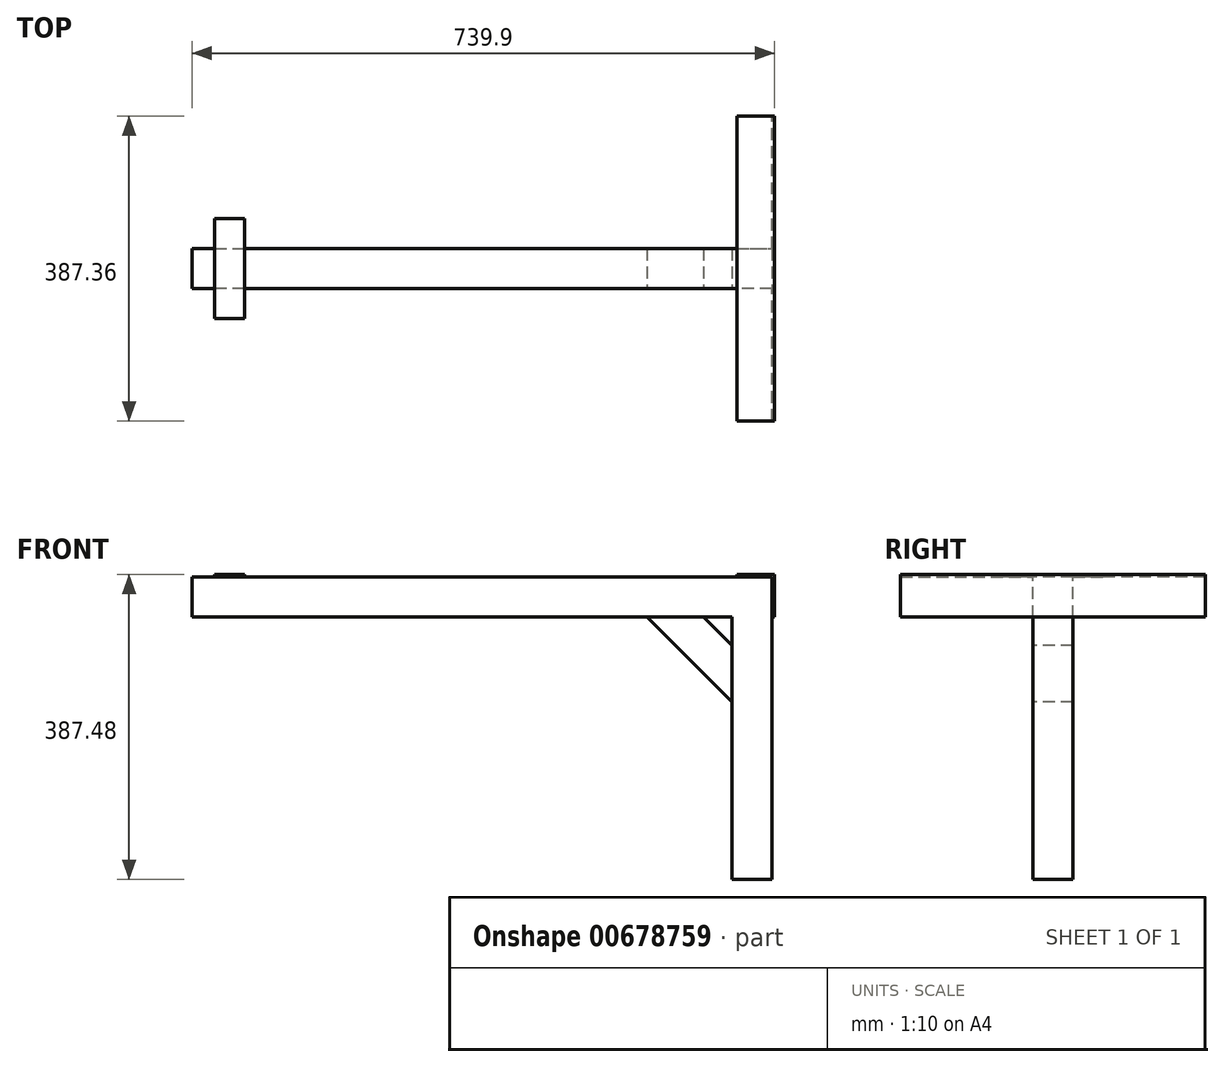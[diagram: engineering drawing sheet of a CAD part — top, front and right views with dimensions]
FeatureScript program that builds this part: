
annotation { "Feature Type Name" : "Feature", "Feature Type Description" : "" }
export const myFeature = defineFeature(function(context is Context, id is Id, definition is map)
    precondition{}
    {
        {
            var Q0;
            Q0=qCreatedBy(makeId("Top.planeOp"),FACE);
            var sketch = newSketch(context, id + "F0", { "sketchPlane" : qUnion([Q0])});
            skLineSegment(sketch, "E0.bottom", {"start": v(25.4, 193.68) * mm, "end": v(-25.4, 193.68) * mm});
            skLineSegment(sketch, "E0.top", {"start": v(25.4, -193.68) * mm, "end": v(-25.4, -193.68) * mm});
            skLineSegment(sketch, "E0.left", {"start": v(25.4, 193.68) * mm, "end": v(25.4, -193.68) * mm});
            skLineSegment(sketch, "E0.right", {"start": v(-25.4, 193.68) * mm, "end": v(-25.4, -193.68) * mm});
            skPoint(sketch, "E0.middle", {"position": v(0, 0) * mm});
            skSolve(sketch);
        }
        {
            var Q0;
            Q0=makeQuery(id+"F0.imprint","IMPRINT",FACE,{"disambiguationData":[TD([[makeQuery(id+"F0.imprint","IMPRINT",EDGE,{"derivedFrom":sQuery(id+"F0.wireOp",EDGE,"E0.bottom")}),1.0]])]});
            extrude(context, id + "F1", {"entities" : qUnion([Q0]), "depth" : 6.35 * mm, "offsetDistance" : 25.4 * mm});
        }
        {
            var Q0;
            Q0=makeQuery(id+"F1.opExtrude","CAP_FACE",FACE,{"disambiguationData":[OSD([sQuery(id+"F0.wireOp",EDGE,"E0.bottom"),sQuery(id+"F0.wireOp",EDGE,"E0.top"),sQuery(id+"F0.wireOp",EDGE,"E0.left"),sQuery(id+"F0.wireOp",EDGE,"E0.right")])],"isStart":true});
            var sketch = newSketch(context, id + "F2", { "sketchPlane" : qUnion([Q0])});
            skLineSegment(sketch, "E1.bottom", {"start": v(25.4, 193.68) * mm, "end": v(19.05, 193.68) * mm});
            skLineSegment(sketch, "E1.top", {"start": v(25.4, -193.68) * mm, "end": v(19.05, -193.68) * mm});
            skLineSegment(sketch, "E1.left", {"start": v(25.4, 193.68) * mm, "end": v(25.4, -193.68) * mm});
            skLineSegment(sketch, "E1.right", {"start": v(19.05, 193.68) * mm, "end": v(19.05, -193.68) * mm});
            skSolve(sketch);
        }
        {
            var Q0;
            Q0=makeQuery(id+"F2.imprint","IMPRINT",FACE,{"disambiguationData":[TD([[makeQuery(id+"F2.imprint","IMPRINT",EDGE,{"derivedFrom":sQuery(id+"F2.wireOp",EDGE,"E1.bottom")}),1.0]])]});
            extrude(context, id + "F3", {"entities" : qUnion([Q0]), "operationType" : NewBodyOperationType.ADD, "depth" : 50.8 * mm, "offsetDistance" : 25.4 * mm});
        }
        {
            var Q0;
            Q0=makeQuery(id+"F3.boolean.opBoolean","MERGE",FACE,{"derivedFrom":[makeQuery(id+"F1.opExtrude","SWEPT_FACE",FACE,{"disambiguationData":[OSD([sQuery(id+"F0.wireOp",EDGE,"E0.left")])]}),makeQuery(id+"F3.opExtrude","SWEPT_FACE",FACE,{"disambiguationData":[OSD([sQuery(id+"F2.wireOp",EDGE,"E1.left")])]})]});
            extrude(context, id + "F4", {"entities" : qUnion([Q0]), "operationType" : NewBodyOperationType.REMOVE, "oppositeDirection" : true, "depth" : 3.05 * mm, "offsetDistance" : 25.4 * mm});
        }
        {
            var Q0;
            Q0=makeQuery(id+"F1.opExtrude","CAP_FACE",FACE,{"disambiguationData":[OSD([sQuery(id+"F0.wireOp",EDGE,"E0.bottom"),sQuery(id+"F0.wireOp",EDGE,"E0.top"),sQuery(id+"F0.wireOp",EDGE,"E0.left"),sQuery(id+"F0.wireOp",EDGE,"E0.right")])],"isStart":false});
            extrude(context, id + "F5", {"entities" : qUnion([Q0]), "operationType" : NewBodyOperationType.REMOVE, "oppositeDirection" : true, "depth" : 3.05 * mm, "offsetDistance" : 25.4 * mm});
        }
        {
            var Q0;
            Q0=makeQuery(id+"F1.opExtrude","CAP_FACE",FACE,{"disambiguationData":[OSD([sQuery(id+"F0.wireOp",EDGE,"E0.bottom"),sQuery(id+"F0.wireOp",EDGE,"E0.top"),sQuery(id+"F0.wireOp",EDGE,"E0.left"),sQuery(id+"F0.wireOp",EDGE,"E0.right")])],"isStart":true});
            var sketch = newSketch(context, id + "F6", { "sketchPlane" : qUnion([Q0])});
            skLineSegment(sketch, "E2", {"start": v(19.05, 0) * mm, "end": v(19.05, 25.4) * mm});
            skLineSegment(sketch, "E3", {"start": v(19.05, 25.4) * mm, "end": v(-717.55, 25.4) * mm});
            skLineSegment(sketch, "E4", {"start": v(-717.55, 25.4) * mm, "end": v(-717.55, -25.4) * mm});
            skLineSegment(sketch, "E5", {"start": v(-717.55, -25.4) * mm, "end": v(19.05, -25.4) * mm});
            skLineSegment(sketch, "E6", {"start": v(19.05, -25.4) * mm, "end": v(19.05, 25.4) * mm});
            skSolve(sketch);
        }
        {
            var Q0;
            {var subQ1=sQuery(id+"F6.wireOp",EDGE,"E3");var subQ4=makeQuery(id+"F1.opExtrude","CAP_EDGE",EDGE,{"disambiguationData":[OSD([sQuery(id+"F0.wireOp",EDGE,"E0.right")])],"isStart":true});var subQ5=makeQuery(id+"F6.imprint","INTERSECT",VERTEX,{"derivedFrom":[subQ4,subQ1]});Q0=makeQuery(id+"F6.imprint","IMPRINT",FACE,{"disambiguationData":[TD([[makeQuery(id+"F6.imprint","IMPRINT",EDGE,{"disambiguationData":[TD([[subQ5,1.0]])],"derivedFrom":subQ4}),-1.0]])]});}
            var Q1;
            {var subQ0=sQuery(id+"F6.wireOp",EDGE,"E4");Q1=makeQuery(id+"F6.imprint","IMPRINT",FACE,{"disambiguationData":[TD([[makeQuery(id+"F6.imprint","IMPRINT",EDGE,{"derivedFrom":subQ0}),1.0]])]});}
            extrude(context, id + "F7", {"entities" : qUnion([Q0, Q1]), "operationType" : NewBodyOperationType.ADD, "depth" : 50.8 * mm, "offsetDistance" : 25.4 * mm});
        }
        {
            var Q0;
            Q0=makeQuery(id+"F7.opExtrude","CAP_FACE",FACE,{"disambiguationData":[OSD([sQuery(id+"F6.wireOp",EDGE,"E3"),sQuery(id+"F6.wireOp",EDGE,"E4"),sQuery(id+"F6.wireOp",EDGE,"E5"),sQuery(id+"F6.wireOp",EDGE,"E6")])],"isStart":true});
            var sketch = newSketch(context, id + "F8", { "sketchPlane" : qUnion([Q0])});
            skLineSegment(sketch, "E7", {"start": v(-717.55, 25.4) * mm, "end": v(-688.85, 25.4) * mm});
            skLineSegment(sketch, "E8", {"start": v(-688.85, 25.4) * mm, "end": v(-688.85, 63.5) * mm});
            skLineSegment(sketch, "E9", {"start": v(-688.85, 63.5) * mm, "end": v(-650.75, 63.5) * mm});
            skLineSegment(sketch, "E10", {"start": v(-650.75, 63.5) * mm, "end": v(-650.75, -25.4) * mm});
            skLineSegment(sketch, "E11", {"start": v(-650.75, -25.4) * mm, "end": v(-650.75, -63.5) * mm});
            skLineSegment(sketch, "E12", {"start": v(-650.75, -63.5) * mm, "end": v(-688.85, -63.5) * mm});
            skLineSegment(sketch, "E13", {"start": v(-688.85, -63.5) * mm, "end": v(-688.85, 25.4) * mm});
            skSolve(sketch);
        }
        {
            var Q0;
            {var subQ0=sQuery(id+"F8.wireOp",EDGE,"E11");Q0=makeQuery(id+"F8.imprint","IMPRINT",FACE,{"disambiguationData":[TD([[makeQuery(id+"F8.imprint","IMPRINT",EDGE,{"derivedFrom":subQ0}),-1.0]])]});}
            var Q1;
            {var subQ0=sQuery(id+"F8.wireOp",EDGE,"E10");var subQ1=sQuery(id+"F6.wireOp",EDGE,"E3");var subQ2=sQuery(id+"F6.wireOp",EDGE,"E5");var subQ3=makeQuery(id+"F7.opExtrude","CAP_FACE",FACE,{"disambiguationData":[OSD([subQ1,sQuery(id+"F6.wireOp",EDGE,"E4"),subQ2,sQuery(id+"F6.wireOp",EDGE,"E6")])],"isStart":true});var subQ6=makeQuery(id+"F7.boolean.opBoolean","SPLIT",EDGE,{"disambiguationData":[topologyDisambiguationEdgeConnected([subQ3])],"derivedFrom":makeQuery(id+"F7.opExtrude","CAP_EDGE",EDGE,{"disambiguationData":[OSD([subQ2])],"isStart":true})});var subQ7=makeQuery(id+"F8.imprint","INTERSECT",VERTEX,{"derivedFrom":[subQ6,subQ0]});Q1=makeQuery(id+"F8.imprint","IMPRINT",FACE,{"disambiguationData":[TD([[makeQuery(id+"F8.imprint","IMPRINT",EDGE,{"disambiguationData":[TD([[subQ7,-1.0]])],"derivedFrom":subQ0}),-1.0]])]});}
            var Q2;
            {var subQ0=sQuery(id+"F8.wireOp",EDGE,"E8");Q2=makeQuery(id+"F8.imprint","IMPRINT",FACE,{"disambiguationData":[TD([[makeQuery(id+"F8.imprint","IMPRINT",EDGE,{"derivedFrom":subQ0}),-1.0]])]});}
            extrude(context, id + "F9", {"entities" : qUnion([Q0, Q1, Q2]), "operationType" : NewBodyOperationType.ADD, "depth" : 3.05 * mm, "offsetDistance" : 25.4 * mm});
        }
        {
            var Q0;
            Q0=makeQuery(id+"F7.boolean.opBoolean","MERGE",FACE,{"derivedFrom":[makeQuery(id+"F3.opExtrude","CAP_FACE",FACE,{"disambiguationData":[OSD([sQuery(id+"F2.wireOp",EDGE,"E1.bottom"),sQuery(id+"F2.wireOp",EDGE,"E1.top"),sQuery(id+"F2.wireOp",EDGE,"E1.left"),sQuery(id+"F2.wireOp",EDGE,"E1.right")])],"isStart":false}),makeQuery(id+"F7.opExtrude","CAP_FACE",FACE,{"disambiguationData":[OSD([sQuery(id+"F6.wireOp",EDGE,"E3"),sQuery(id+"F6.wireOp",EDGE,"E4"),sQuery(id+"F6.wireOp",EDGE,"E5"),sQuery(id+"F6.wireOp",EDGE,"E6")])],"isStart":false})]});
            var sketch = newSketch(context, id + "F10", { "sketchPlane" : qUnion([Q0])});
            skLineSegment(sketch, "E14", {"start": v(19.05, -25.4) * mm, "end": v(19.05, 25.4) * mm});
            skLineSegment(sketch, "E15", {"start": v(19.05, 25.4) * mm, "end": v(-31.75, 25.4) * mm});
            skLineSegment(sketch, "E16", {"start": v(-31.75, 25.4) * mm, "end": v(-31.75, -25.4) * mm});
            skLineSegment(sketch, "E17", {"start": v(-31.75, -25.4) * mm, "end": v(19.05, -25.4) * mm});
            skSolve(sketch);
        }
        {
            var Q0;
            Q0=qSketchRegion(id+"F10",true);
            extrude(context, id + "F11", {"entities" : qUnion([Q0]), "operationType" : NewBodyOperationType.ADD, "depth" : 333.38 * mm, "offsetDistance" : 25.4 * mm});
        }
        {
            var Q0;
            Q0=makeQuery(id+"F11.boolean.opBoolean","MERGE",FACE,{"derivedFrom":[makeQuery(id+"F7.opExtrude","SWEPT_FACE",FACE,{"disambiguationData":[OSD([sQuery(id+"F6.wireOp",EDGE,"E3")])]}),makeQuery(id+"F11.opExtrude","SWEPT_FACE",FACE,{"disambiguationData":[OSD([sQuery(id+"F10.wireOp",EDGE,"E15")])]})]});
            var sketch = newSketch(context, id + "F12", { "sketchPlane" : qUnion([Q0])});
            skLineSegment(sketch, "E18", {"start": v(-31.75, -50.8) * mm, "end": v(-139.7, -50.8) * mm});
            skLineSegment(sketch, "E19", {"start": v(-31.75, -158.75) * mm, "end": v(-139.7, -50.8) * mm});
            skLineSegment(sketch, "E20", {"start": v(-49.8, -68.85) * mm, "end": v(-67.76, -50.9) * mm});
            skPoint(sketch, "E20.endSnap0", {"position": v(-67.76, -86.81) * mm});
            skLineSegment(sketch, "E21", {"start": v(-67.76, -50.9) * mm, "end": v(-31.75, -86.9) * mm});
            skLineSegment(sketch, "E22", {"start": v(-139.7, -50.8) * mm, "end": v(-67.76, -50.9) * mm});
            skLineSegment(sketch, "E23", {"start": v(-31.75, -86.9) * mm, "end": v(-31.75, -158.75) * mm});
            skSolve(sketch);
        }
        {
            var Q0;
            Q0=makeQuery(id+"F12.imprint","IMPRINT",FACE,{"disambiguationData":[TD([[makeQuery(id+"F12.imprint","IMPRINT",EDGE,{"derivedFrom":sQuery(id+"F12.wireOp",EDGE,"E19")}),-1.0]])]});
            extrude(context, id + "F13", {"entities" : qUnion([Q0]), "oppositeDirection" : true, "depth" : 50.8 * mm, "offsetDistance" : 25.4 * mm});
        }
    });
